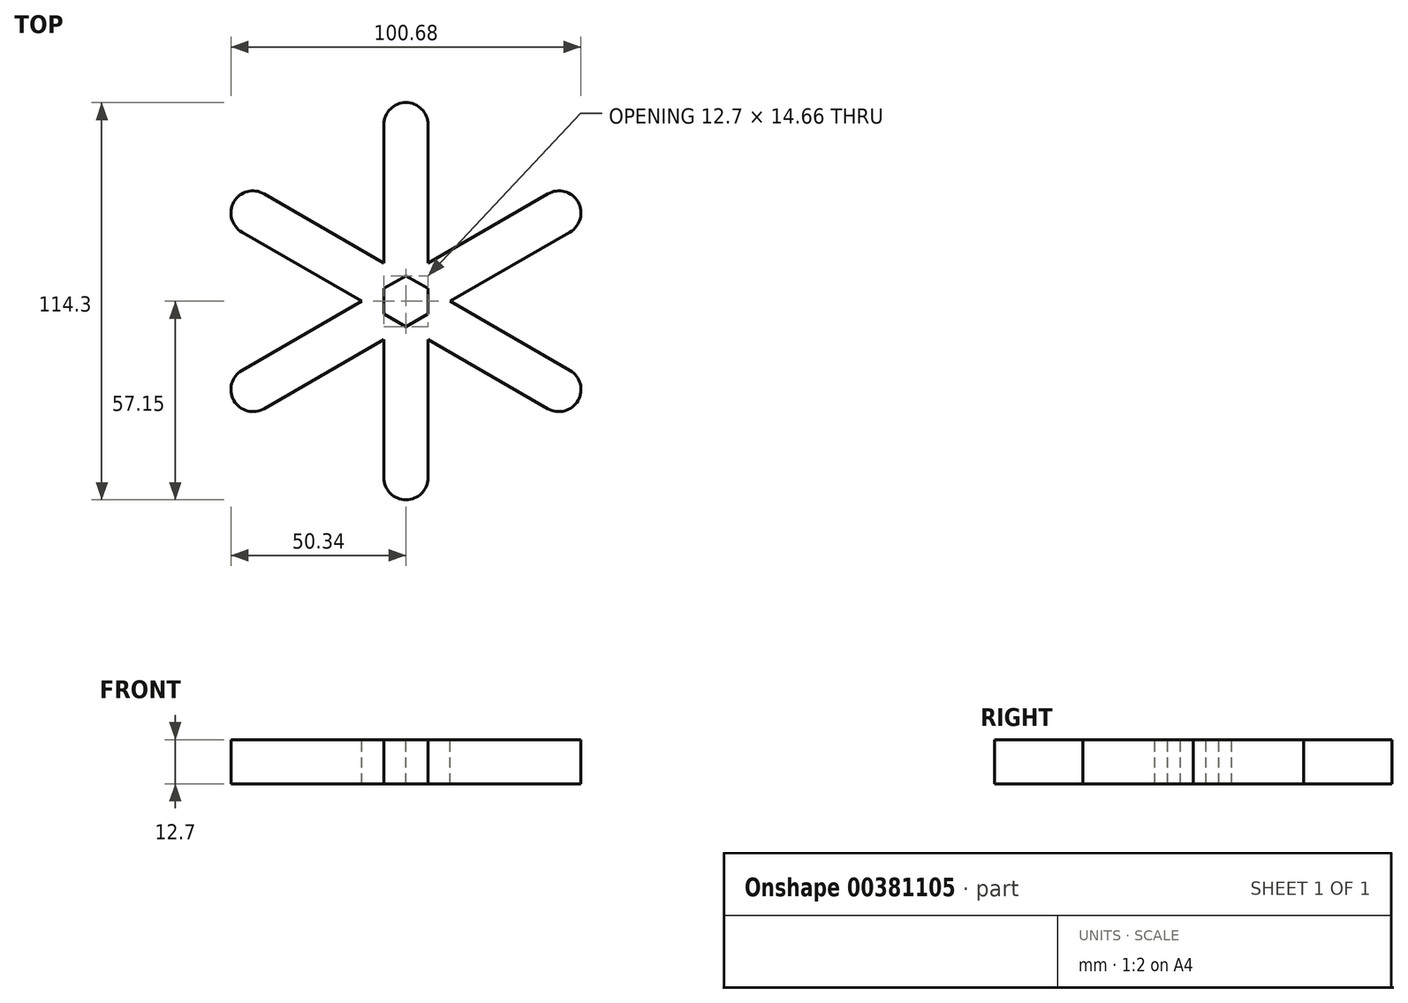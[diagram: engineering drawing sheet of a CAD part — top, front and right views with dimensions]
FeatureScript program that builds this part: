
annotation { "Feature Type Name" : "Feature", "Feature Type Description" : "" }
export const myFeature = defineFeature(function(context is Context, id is Id, definition is map)
    precondition{}
    {
        {
            var Q0;
            Q0=qCreatedBy(makeId("Top.planeOp"),FACE);
            var sketch = newSketch(context, id + "F0", { "sketchPlane" : qUnion([Q0])});
            skArc(sketch, "E0", {"start": v(-6.35, 0) * mm, "mid": v(0, -6.35) * mm, "end": v(6.35, 0) * mm});
            skLineSegment(sketch, "E1.bottom", {"start": v(-6.35, 0) * mm, "end": v(6.35, 0) * mm});
            skLineSegment(sketch, "E1.left", {"start": v(-6.35, 0) * mm, "end": v(-6.35, 50.8) * mm});
            skLineSegment(sketch, "E1.right", {"start": v(6.35, 0) * mm, "end": v(6.35, 50.8) * mm});
            skArc(sketch, "E2", {"start": v(6.35, 50.8) * mm, "mid": v(0, 57.15) * mm, "end": v(-6.35, 50.8) * mm});
            skLineSegment(sketch, "E3.1.0", {"start": v(-3.18, -5.5) * mm, "end": v(-47.17, 19.9) * mm});
            skLineSegment(sketch, "E3.1.1", {"start": v(3.18, 5.5) * mm, "end": v(-40.82, 30.9) * mm});
            skArc(sketch, "E3.1.2", {"start": v(-40.82, 30.9) * mm, "mid": v(-49.5, 28.57) * mm, "end": v(-47.17, 19.9) * mm});
            skLineSegment(sketch, "E3.2.0", {"start": v(3.18, -5.5) * mm, "end": v(-40.82, -30.9) * mm});
            skLineSegment(sketch, "E3.2.1", {"start": v(-3.17, 5.5) * mm, "end": v(-47.17, -19.9) * mm});
            skArc(sketch, "E3.2.2", {"start": v(-47.17, -19.9) * mm, "mid": v(-49.5, -28.57) * mm, "end": v(-40.82, -30.9) * mm});
            skLineSegment(sketch, "E3.3.0", {"start": v(6.35, 0) * mm, "end": v(6.35, -50.8) * mm});
            skLineSegment(sketch, "E3.3.1", {"start": v(-6.35, 0) * mm, "end": v(-6.35, -50.8) * mm});
            skArc(sketch, "E3.3.2", {"start": v(-6.35, -50.8) * mm, "mid": v(0, -57.15) * mm, "end": v(6.35, -50.8) * mm});
            skLineSegment(sketch, "E3.4.0", {"start": v(3.18, 5.5) * mm, "end": v(47.17, -19.9) * mm});
            skLineSegment(sketch, "E3.4.1", {"start": v(-3.18, -5.5) * mm, "end": v(40.82, -30.9) * mm});
            skArc(sketch, "E3.4.2", {"start": v(40.82, -30.9) * mm, "mid": v(49.5, -28.58) * mm, "end": v(47.17, -19.9) * mm});
            skLineSegment(sketch, "E3.5.0", {"start": v(-3.18, 5.5) * mm, "end": v(40.82, 30.9) * mm});
            skLineSegment(sketch, "E3.5.1", {"start": v(3.17, -5.5) * mm, "end": v(47.17, 19.9) * mm});
            skArc(sketch, "E3.5.2", {"start": v(47.17, 19.9) * mm, "mid": v(49.5, 28.58) * mm, "end": v(40.82, 30.9) * mm});
            skSolve(sketch);
        }
        {
            var Q0;
            Q0 = qSketchRegion(id + "F0", true);
            extrude(context, id + "F1", {"entities" : qUnion([Q0]), "oppositeDirection" : true, "depth" : 12.7 * mm});
        }
        {
            var Q0;
            Q0=qCreatedBy(makeId("Top.planeOp"),FACE);
            cPlane(context, id + "F2", {"entities" : qUnion([Q0]), "cplaneType" : CPlaneType.OFFSET, "offset" : 25.4 * mm, "width" : 152.4 * mm, "height" : 152.4 * mm});
        }
    });
